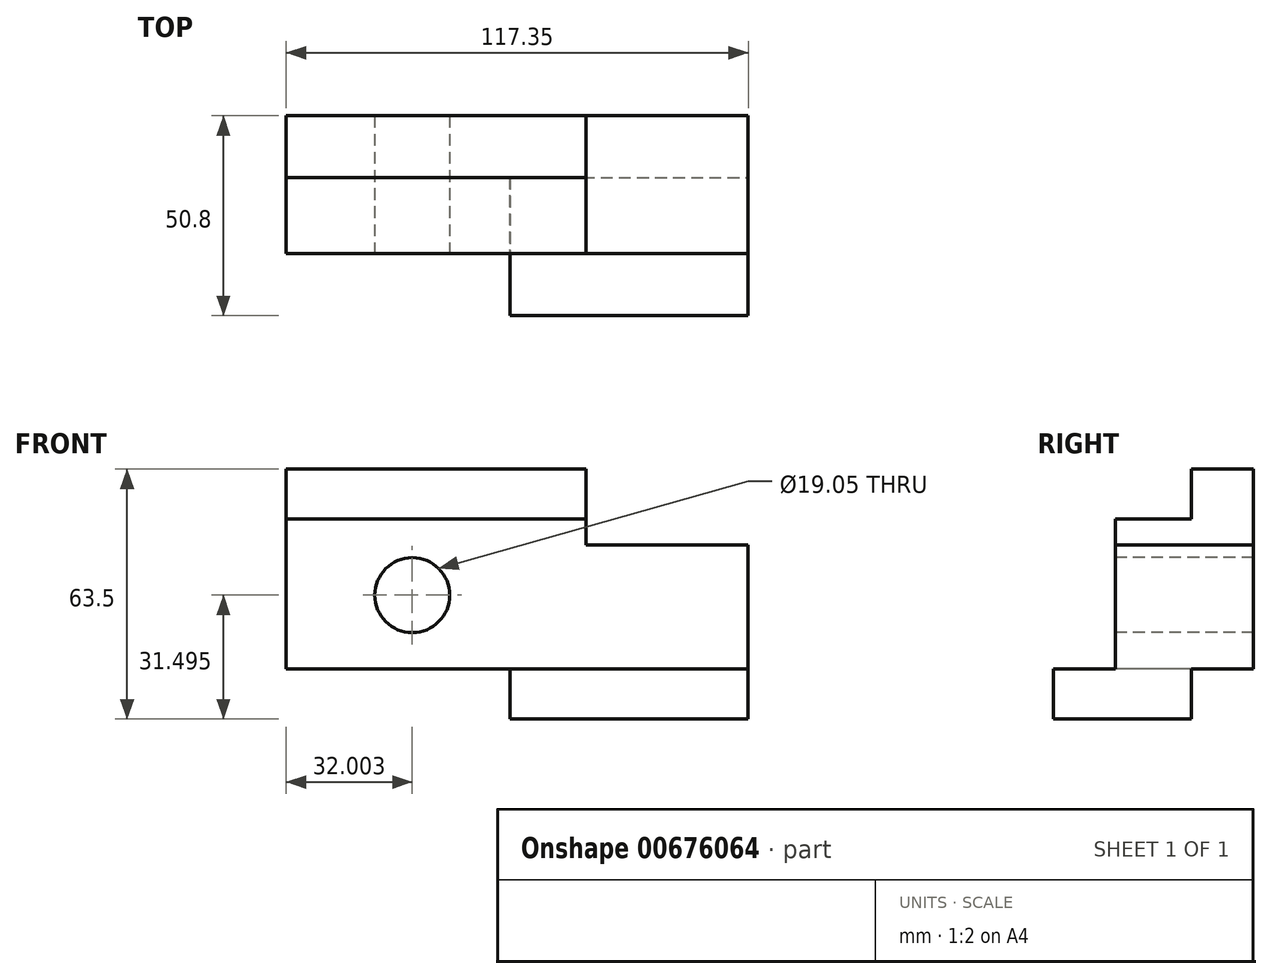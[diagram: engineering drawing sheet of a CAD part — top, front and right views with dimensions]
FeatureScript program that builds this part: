
annotation { "Feature Type Name" : "Feature", "Feature Type Description" : "" }
export const myFeature = defineFeature(function(context is Context, id is Id, definition is map)
    precondition{}
    {
        {
            var Q0;
            Q0=qCreatedBy(makeId("Front.planeOp"),FACE);
            var sketch = newSketch(context, id + "F0", { "sketchPlane" : qUnion([Q0])});
            skLineSegment(sketch, "E0.bottom", {"start": v(-53.71, 38.74) * mm, "end": v(63.64, 38.74) * mm});
            skLineSegment(sketch, "E0.top", {"start": v(-53.71, -24.76) * mm, "end": v(63.64, -24.76) * mm});
            skLineSegment(sketch, "E0.left", {"start": v(-53.71, 38.74) * mm, "end": v(-53.71, -24.76) * mm});
            skLineSegment(sketch, "E0.right", {"start": v(63.64, 38.74) * mm, "end": v(63.64, -24.76) * mm});
            skSolve(sketch);
        }
        {
            var Q0;
            Q0=makeQuery(id+"F0.imprint","IMPRINT",FACE,{"disambiguationData":[TD([[makeQuery(id+"F0.imprint","IMPRINT",EDGE,{"derivedFrom":sQuery(id+"F0.wireOp",EDGE,"E0.bottom")}),-1.0]])]});
            extrude(context, id + "F1", {"entities" : qUnion([Q0]), "depth" : 35.05 * mm, "offsetDistance" : 25.4 * mm});
        }
        {
            var Q0;
            Q0=makeQuery(id+"F1.opExtrude","CAP_FACE",FACE,{"disambiguationData":[OSD([sQuery(id+"F0.wireOp",EDGE,"E0.bottom"),sQuery(id+"F0.wireOp",EDGE,"E0.top"),sQuery(id+"F0.wireOp",EDGE,"E0.left"),sQuery(id+"F0.wireOp",EDGE,"E0.right")])],"isStart":false});
            var sketch = newSketch(context, id + "F2", { "sketchPlane" : qUnion([Q0])});
            skLineSegment(sketch, "E1.bottom", {"start": v(63.64, -24.76) * mm, "end": v(3.19, -24.76) * mm});
            skLineSegment(sketch, "E1.top", {"start": v(63.64, -12.06) * mm, "end": v(3.19, -12.06) * mm});
            skLineSegment(sketch, "E1.left", {"start": v(63.64, -24.76) * mm, "end": v(63.64, -12.06) * mm});
            skLineSegment(sketch, "E1.right", {"start": v(3.19, -24.76) * mm, "end": v(3.19, -12.06) * mm});
            skLineSegment(sketch, "E2.bottom", {"start": v(-53.71, 38.74) * mm, "end": v(22.49, 38.74) * mm});
            skLineSegment(sketch, "E2.top", {"start": v(-53.71, 26.04) * mm, "end": v(22.49, 26.04) * mm});
            skLineSegment(sketch, "E2.left", {"start": v(-53.71, 38.74) * mm, "end": v(-53.71, 26.04) * mm});
            skLineSegment(sketch, "E2.right", {"start": v(22.49, 38.74) * mm, "end": v(22.49, 26.04) * mm});
            skLineSegment(sketch, "E3.bottom", {"start": v(-53.71, -24.76) * mm, "end": v(3.19, -24.76) * mm});
            skLineSegment(sketch, "E3.top", {"start": v(-53.71, -12.06) * mm, "end": v(3.19, -12.06) * mm});
            skLineSegment(sketch, "E3.left", {"start": v(-53.71, -24.76) * mm, "end": v(-53.71, -12.06) * mm});
            skSolve(sketch);
        }
        {
            var Q0;
            Q0=makeQuery(id+"F2.imprint","IMPRINT",FACE,{"disambiguationData":[TD([[makeQuery(id+"F2.imprint","IMPRINT",EDGE,{"derivedFrom":sQuery(id+"F2.wireOp",EDGE,"E1.bottom")}),1.0]])]});
            extrude(context, id + "F3", {"entities" : qUnion([Q0]), "operationType" : NewBodyOperationType.ADD, "depth" : 15.75 * mm, "offsetDistance" : 25.4 * mm});
        }
        {
            var Q0;
            Q0=makeQuery(id+"F2.imprint","IMPRINT",FACE,{"disambiguationData":[TD([[makeQuery(id+"F2.imprint","IMPRINT",EDGE,{"derivedFrom":sQuery(id+"F2.wireOp",EDGE,"E3.bottom")}),1.0]])]});
            extrude(context, id + "F4", {"entities" : qUnion([Q0]), "operationType" : NewBodyOperationType.REMOVE, "endBound" : BoundingType.THROUGH_ALL, "oppositeDirection" : true, "depth" : 25.4 * mm, "offsetDistance" : 25.4 * mm});
        }
        {
            var Q0;
            Q0=makeQuery(id+"F2.imprint","IMPRINT",FACE,{"disambiguationData":[TD([[makeQuery(id+"F2.imprint","IMPRINT",EDGE,{"derivedFrom":sQuery(id+"F2.wireOp",EDGE,"E2.bottom")}),-1.0]])]});
            extrude(context, id + "F5", {"entities" : qUnion([Q0]), "operationType" : NewBodyOperationType.REMOVE, "oppositeDirection" : true, "depth" : 19.3 * mm, "offsetDistance" : 25.4 * mm});
        }
        {
            var Q0;
            Q0=makeQuery(id+"F1.opExtrude","CAP_FACE",FACE,{"disambiguationData":[OSD([sQuery(id+"F0.wireOp",EDGE,"E0.bottom"),sQuery(id+"F0.wireOp",EDGE,"E0.top"),sQuery(id+"F0.wireOp",EDGE,"E0.left"),sQuery(id+"F0.wireOp",EDGE,"E0.right")])],"isStart":false});
            var sketch = newSketch(context, id + "F6", { "sketchPlane" : qUnion([Q0])});
            skLineSegment(sketch, "E4.bottom", {"start": v(63.64, 38.74) * mm, "end": v(22.49, 38.74) * mm});
            skLineSegment(sketch, "E4.top", {"start": v(63.64, 19.44) * mm, "end": v(22.49, 19.44) * mm});
            skLineSegment(sketch, "E4.left", {"start": v(63.64, 38.74) * mm, "end": v(63.64, 19.44) * mm});
            skLineSegment(sketch, "E4.right", {"start": v(22.49, 38.74) * mm, "end": v(22.49, 19.44) * mm});
            skSolve(sketch);
        }
        {
            var Q0;
            Q0 = qSketchRegion(id + "F6", true);
            extrude(context, id + "F7", {"entities" : qUnion([Q0]), "operationType" : NewBodyOperationType.REMOVE, "endBound" : BoundingType.THROUGH_ALL, "oppositeDirection" : true, "depth" : 25.4 * mm, "offsetDistance" : 25.4 * mm});
        }
        {
            var Q0;
            Q0=makeQuery(id+"F3.boolean.opBoolean","MERGE",FACE,{"derivedFrom":[makeQuery(id+"F1.opExtrude","SWEPT_FACE",FACE,{"disambiguationData":[OSD([sQuery(id+"F0.wireOp",EDGE,"E0.right")])]}),makeQuery(id+"F3.opExtrude","SWEPT_FACE",FACE,{"disambiguationData":[OSD([sQuery(id+"F2.wireOp",EDGE,"E1.left")])]})]});
            var sketch = newSketch(context, id + "F8", { "sketchPlane" : qUnion([Q0])});
            skLineSegment(sketch, "E5.bottom", {"start": v(0, -24.76) * mm, "end": v(-15.75, -24.76) * mm});
            skLineSegment(sketch, "E5.top", {"start": v(0, -12.06) * mm, "end": v(-15.75, -12.06) * mm});
            skLineSegment(sketch, "E5.left", {"start": v(0, -24.76) * mm, "end": v(0, -12.06) * mm});
            skLineSegment(sketch, "E5.right", {"start": v(-15.75, -24.76) * mm, "end": v(-15.75, -12.06) * mm});
            skSolve(sketch);
        }
        {
            var Q0;
            Q0=makeQuery(id+"F8.imprint","IMPRINT",FACE,{"disambiguationData":[TD([[makeQuery(id+"F8.imprint","IMPRINT",EDGE,{"derivedFrom":sQuery(id+"F8.wireOp",EDGE,"E5.bottom")}),1.0]])]});
            extrude(context, id + "F9", {"entities" : qUnion([Q0]), "operationType" : NewBodyOperationType.REMOVE, "endBound" : BoundingType.THROUGH_ALL, "oppositeDirection" : true, "depth" : 25.4 * mm, "offsetDistance" : 25.4 * mm});
        }
        {
            var Q0;
            Q0=makeQuery(id+"F1.opExtrude","CAP_FACE",FACE,{"disambiguationData":[OSD([sQuery(id+"F0.wireOp",EDGE,"E0.bottom"),sQuery(id+"F0.wireOp",EDGE,"E0.top"),sQuery(id+"F0.wireOp",EDGE,"E0.left"),sQuery(id+"F0.wireOp",EDGE,"E0.right")])],"isStart":false});
            var sketch = newSketch(context, id + "F10", { "sketchPlane" : qUnion([Q0])});
            skCircle(sketch, "E6", {"center": v(-21.7, 6.74) * mm, "radius": 9.52 * mm});
            skSolve(sketch);
        }
        {
            var Q0;
            Q0=makeQuery(id+"F10.imprint","IMPRINT",FACE,{"disambiguationData":[TD([[makeQuery(id+"F10.imprint","IMPRINT",EDGE,{"derivedFrom":sQuery(id+"F10.wireOp",EDGE,"E6")}),1.0]])]});
            extrude(context, id + "F11", {"entities" : qUnion([Q0]), "operationType" : NewBodyOperationType.REMOVE, "endBound" : BoundingType.THROUGH_ALL, "oppositeDirection" : true, "depth" : 25.4 * mm, "offsetDistance" : 25.4 * mm});
        }
    });
